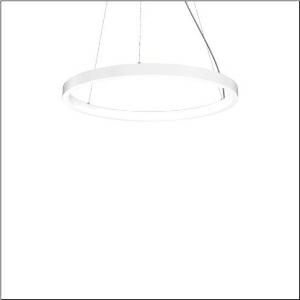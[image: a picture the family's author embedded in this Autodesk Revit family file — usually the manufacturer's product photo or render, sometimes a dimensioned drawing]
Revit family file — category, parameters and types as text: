
# Revit family: silica_21_ring-i_5pjbi3d3004a
name_source: partatom
category: Lighting Fixtures
units: mm (PartAtom-declared; Revit-internal decimal feet)

## family parameters
Cut with Voids When Loaded = No
Host = Face
Light Source = No
Part Type = Normal
Room Calculation Point = No
Round Connector Dimension = Use Diameter
Shared = No

## types (1)
- Silica 21 Ring-I (1 x LED, 6430 lm, 105 W, 4000K)
    Apparent Load = 105 VA
    CIE Flux Codes = 22 48 76 50 101
    Color Rendering = 80
    Color Temperature = 4000K
    Default Elevation = 1800 mm
    Description = Silica 21 Ring-I, suspended luminaire, of PMMA, frosted, light emission: inner ring side luminous distribution, primary light characteristic: symmetric, installation type: suspended mounting, LED, rated luminous flux: 6.430lm, luminous efficacy: 61lm/W, light colour: 840, colour temperature: 4000K, control gear: DALI 2, with terminal, 5-pole, mains connection: 230V, AC/DC, 0/50..60Hz, rated input power: 105W, housing, of extruded aluminium section, traffic white (RAL 9016), diameter: 1.090mm, ceiling canopy, traffic white (RAL 9016), protection rating (lamp compartment): IP40, insulation class (complete): insulation class I (protective earthing), certification: CE, impact resistance: IK02, permissible operating ambient temperature: 0..+35°C, packaging unit: 1 piece
    Height = 48 mm  [stored 0.15748 ft]
    Lamp = 1 x LED
    Lamp Light Flux = 6430 lm
    Lamp Power = 105 W
    Lamp count = 1
    Length = 1090 mm
    Luminous efficacy = 61 lm/W
    Manufacturer = Siteco
    ModVariant = No
    Model = 5PJBI3D3004A
    Mounting Place = Ceiling
    Mounting Type = Pendant
    Number of Poles = 1
    OnlyDefault = Yes
    Power Factor = 1
    Product Name = Silica 21 Ring-I
    Product group = suspended luminaire
    ProductGroupID = 904
    Protection Class = Protection class I
    Protection Degree = IP 40
    RLX_Detail_Level = 1
    RLX_Emergency_Light_Flux = 0 lm
    RLX_Emergency_Type = 0
    RLX_Emergency_Type_DB = No
    RlxData = <blob elided: 12793 chars, md5=955e0a6a>
    Socket = socket
    Standby Power = 0 W
    System Light Flux = 6430 lm
    System Power = 105 W
    Type Comments = Product without accessories
    Type Image = l_1258371.jpg
    URL = http://relux.com
    VarID = ---
    Voltage = 0 V
    Weight = 0.00 kg
    Width = 0 mm  [stored 0 ft]

note: [stored X ft] marks values corroborated as IEEE doubles in the binary element streams (Revit-internal decimal feet)

## geometry (parser evidence)
native form markers: Sweep x9
no freeform markers — native parametric forms only
